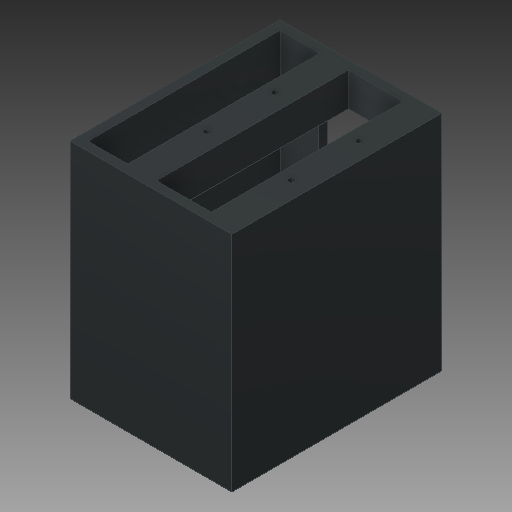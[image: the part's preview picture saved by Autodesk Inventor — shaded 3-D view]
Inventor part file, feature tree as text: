
AUTODESK INVENTOR PART (.ipt)
format: ipt  version: 2018 (Build 220112000, 112)  size: 173,568 bytes
history: native  units: mm
features: extrude x6, sketch x6
ambient origin geometry x8: Origin, YZ Plane, XZ Plane, XY Plane, X Axis, Y Axis, Z Axis, Center Point
bodies: Body1 (feature_tree)
feature tree (12):
  extrude  "Extrusion2"  Depth=548.0mm
  extrude  "Extrusion3"  Depth=583.0mm TaperAngle=0.0deg
  extrude  "Extrusion4"  Depth=345.0mm
  extrude  "Extrusion5"  Depth=88.0mm
  extrude  "Extrusion6"  Depth=75.0mm
  extrude  "Extrusion7"  Depth=583.0mm TaperAngle=0.0deg
  sketch  "Sketch1"  dims[d0=422.0mm d1=548.0mm]
  sketch  "Sketch2"  dims[d4=23.0mm d5=583.0mm d6=0.0mm]
  sketch  "Sketch3"  dims[d7=210.0mm d8=345.0mm]
  sketch  "Sketch4"  dims[d9=88.0mm d11=88.0mm]
  sketch  "Sketch5"  dims[d12=583.0mm d13=0.0mm d14=75.0mm]
  sketch  "Sketch6"  dims[d15=104.0mm d16=583.0mm d17=0.0mm d18=54.0mm d19=583.0mm d20=0.0mm d21=16.0mm d22=16.0mm d23=170.0mm d24=200.0mm d25=45.0mm d26=45.0mm d27=170.0mm d28=200.0mm d29=16.0mm d30=16.0mm d31=45.0mm d32=45.0mm d33=16.0mm d34=0.0mm d35=123.0mm d36=0.0mm]
